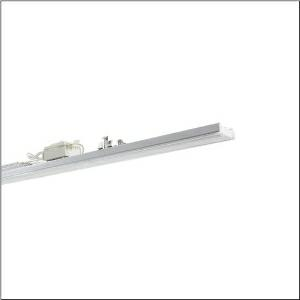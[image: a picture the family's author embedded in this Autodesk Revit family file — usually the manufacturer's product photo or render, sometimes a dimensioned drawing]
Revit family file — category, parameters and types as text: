
# Revit family: licross_21_recessed_mo_52te12dv6fxg
name_source: partatom
category: Lighting Fixtures
units: mm (PartAtom-declared; Revit-internal decimal feet)

## family parameters
Cut with Voids When Loaded = No
Host = Face
Light Source = No
Part Type = Normal
Room Calculation Point = No
Round Connector Dimension = Use Diameter
Shared = No

## types (1)
- --- (1 x LED, 15000 lm, 85.3 W, 6500K)
    Apparent Load = 85 VA
    CIE Flux Codes = 72 92 99 100 100
    Color Rendering = 80
    Color Temperature = 6500K
    Default Elevation = 1800 mm
    Description = Licross 21 Recessed MO, luminaire insert, of sheet steel, galvanised, coil coated, white, length: 2.250mm, width: 66mm, height: 67mm, LED rated luminous flux: 15.000lm, light colour: 865, SDCM (Standard Deviation of Colour Matching)MacAdam ≤ 3 SDCM (initial), control gear: DALI 2, with plug, 5-pole, with phase selection, mains connection: 220..240V, AC, 50/60Hz, rated input power: 85W, internal wiring halogen-free, primary optical cover: cover, of PMMA, light emission: direct distribution, primary light characteristic: symmetric, protection rating (complete): IP54, insulation class (complete): insulation class I (protective earthing), certification: CE, ENEC, VDE, UKCA, protection symbol: D if used in an environment with non-conductive dust loads with corresponding accessories, impact resistance: IK06, permissible ambient temperature for indoor applications: -25..+35°C, corresponds to IFS (International Featured Standards) requirements for safety and quality in the food industry, reducing of maximum allowable ambient temperature of 5°C with ceiling mounting, LABS conformity tested according to VDMA 24364:2018-05, The light source and the operating device comply with the requirements of the Ecodesign Regulation (EU) 2019/2020 and are replaceable in accordance with this regulation, packaging unit: 1 piece
    Height = 58 mm
    Lamp = 1 x LED
    Lamp Light Flux = 15000 lm
    Lamp Power = 85.3 W
    Lamp count = 1
    Length = 2250 mm
    Luminous efficacy = 176 lm/W
    Manufacturer = Siteco
    ModVariant = No
    Model = 52TE12DV6FXG
    Mounting Place = Ceiling
    Mounting Type = Pendant
    Number of Poles = 1
    OnlyDefault = Yes
    Power Factor = 1
    Product Name = Licross 21 Recessed MO
    Product group = luminaire insert | ceiling pendant
    ProductGroupID = 901
    Protection Class = Protection class I
    Protection Degree = IP 54
    RLX_Detail_Level = 1
    RLX_Emergency_Light_Flux = 0 lm
    RLX_Emergency_Type = 0
    RLX_Emergency_Type_DB = No
    RlxData = <blob elided: 29949 chars, md5=a786ab8e>
    Socket = socket
    Standby Power = 0 W
    System Light Flux = 15000 lm
    System Power = 85 W
    Type Comments = factory setting: luminous flux: 100 % | dim-lin: 254 | 390 mA
    Type Image = l_1296930.jpg
    URL = http://relux.com
    VarID = @adj_093377
    Voltage = 0 V
    Weight = 0.00 kg
    Width = 66 mm

## geometry (parser evidence)
native form markers: Blend x4, Sweep x10
no freeform markers — native parametric forms only
